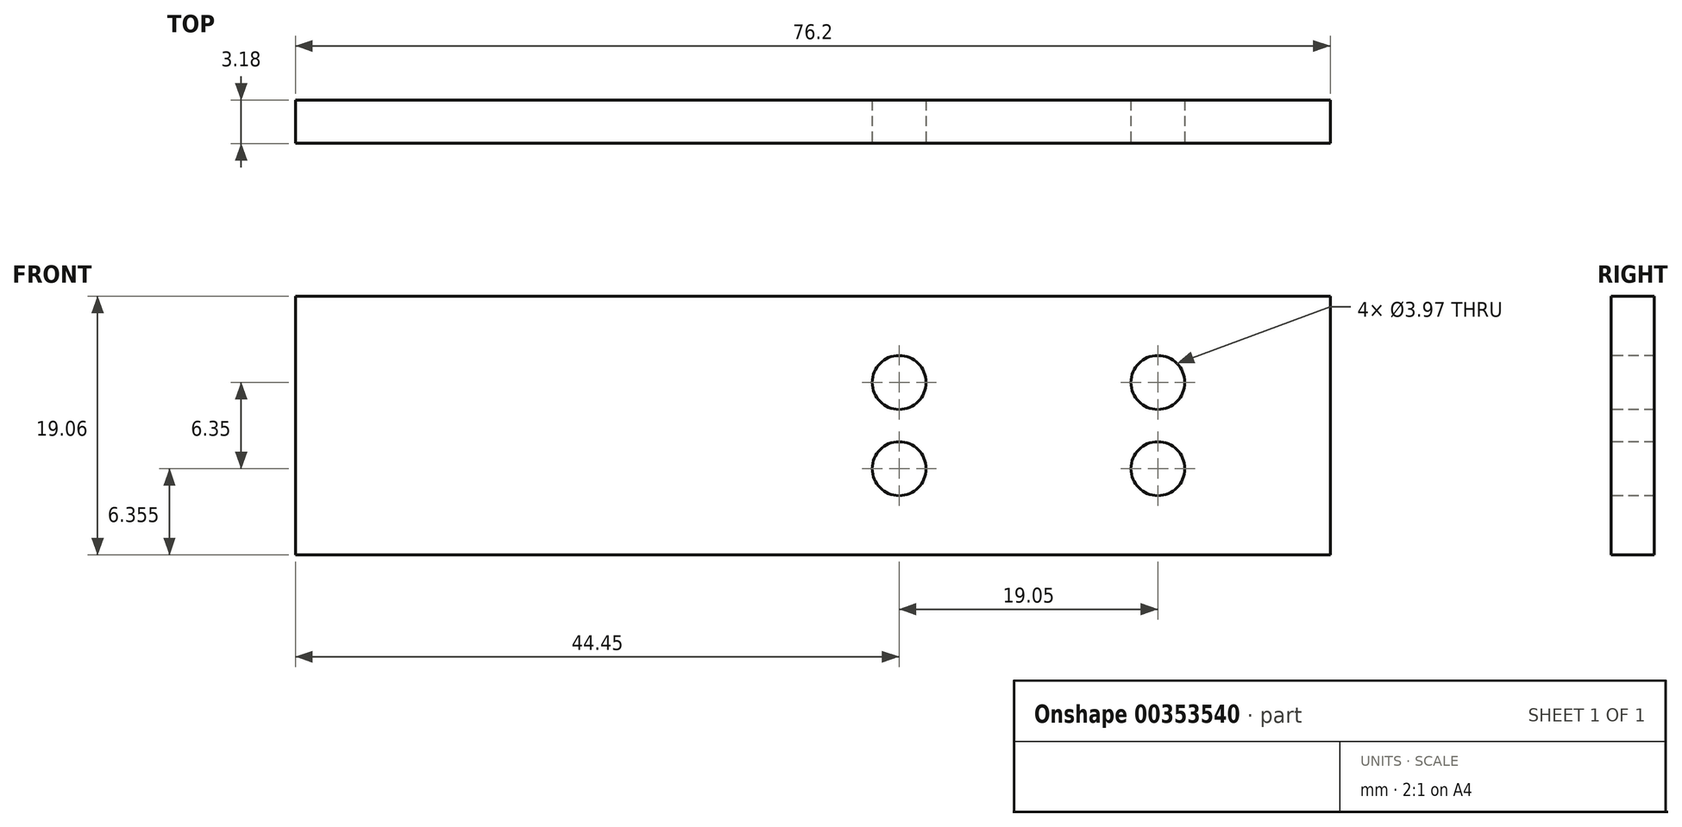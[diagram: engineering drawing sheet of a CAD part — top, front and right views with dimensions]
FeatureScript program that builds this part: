
annotation { "Feature Type Name" : "Feature", "Feature Type Description" : "" }
export const myFeature = defineFeature(function(context is Context, id is Id, definition is map)
    precondition{}
    {
        {
            var Q0;
            Q0=qCreatedBy(makeId("Front.planeOp"),FACE);
            var sketch = newSketch(context, id + "F0", { "sketchPlane" : qUnion([Q0])});
            skLineSegment(sketch, "E0.bottom", {"start": v(38.1, 9.53) * mm, "end": v(-38.1, 9.53) * mm});
            skLineSegment(sketch, "E0.top", {"start": v(38.1, -9.53) * mm, "end": v(-38.1, -9.53) * mm});
            skLineSegment(sketch, "E0.left", {"start": v(38.1, 9.53) * mm, "end": v(38.1, -9.52) * mm});
            skLineSegment(sketch, "E0.right", {"start": v(-38.1, 9.53) * mm, "end": v(-38.1, -9.53) * mm});
            skPoint(sketch, "E0.middle", {"position": v(0, 0) * mm});
            skSolve(sketch);
        }
        {
            var Q0;
            Q0 = qSketchRegion(id + "F0", true);
            extrude(context, id + "F1", {"entities" : qUnion([Q0]), "depth" : 3.17 * mm, "symmetric" : true});
        }
        {
            var Q0;
            Q0=makeQuery(id+"F1.opExtrude","CAP_FACE",FACE,{"disambiguationData":[OSD([sQuery(id+"F0.wireOp",EDGE,"E0.bottom"),sQuery(id+"F0.wireOp",EDGE,"E0.top"),sQuery(id+"F0.wireOp",EDGE,"E0.left"),sQuery(id+"F0.wireOp",EDGE,"E0.right")])],"isStart":false});
            var sketch = newSketch(context, id + "F2", { "sketchPlane" : qUnion([Q0])});
            skCircle(sketch, "E1", {"center": v(6.35, 3.18) * mm, "radius": 1.98 * mm});
            skCircle(sketch, "E2", {"center": v(6.35, -3.17) * mm, "radius": 1.98 * mm});
            skCircle(sketch, "E3", {"center": v(25.4, 3.18) * mm, "radius": 1.98 * mm});
            skCircle(sketch, "E4", {"center": v(25.4, -3.17) * mm, "radius": 1.98 * mm});
            skSolve(sketch);
        }
        {
            var Q0;
            Q0=makeQuery(id+"F2.imprint","IMPRINT",FACE,{"disambiguationData":[TD([[makeQuery(id+"F2.imprint","IMPRINT",EDGE,{"derivedFrom":sQuery(id+"F2.wireOp",EDGE,"E1")}),1.0]])]});
            var Q1;
            Q1=makeQuery(id+"F2.imprint","IMPRINT",FACE,{"disambiguationData":[TD([[makeQuery(id+"F2.imprint","IMPRINT",EDGE,{"derivedFrom":sQuery(id+"F2.wireOp",EDGE,"E3")}),1.0]])]});
            var Q2;
            Q2=makeQuery(id+"F2.imprint","IMPRINT",FACE,{"disambiguationData":[TD([[makeQuery(id+"F2.imprint","IMPRINT",EDGE,{"derivedFrom":sQuery(id+"F2.wireOp",EDGE,"E4")}),1.0]])]});
            var Q3;
            Q3=makeQuery(id+"F2.imprint","IMPRINT",FACE,{"disambiguationData":[TD([[makeQuery(id+"F2.imprint","IMPRINT",EDGE,{"derivedFrom":sQuery(id+"F2.wireOp",EDGE,"E2")}),1.0]])]});
            extrude(context, id + "F3", {"entities" : qUnion([Q0, Q1, Q2, Q3]), "operationType" : NewBodyOperationType.REMOVE, "oppositeDirection" : true, "depth" : 3.17 * mm});
        }
    });
